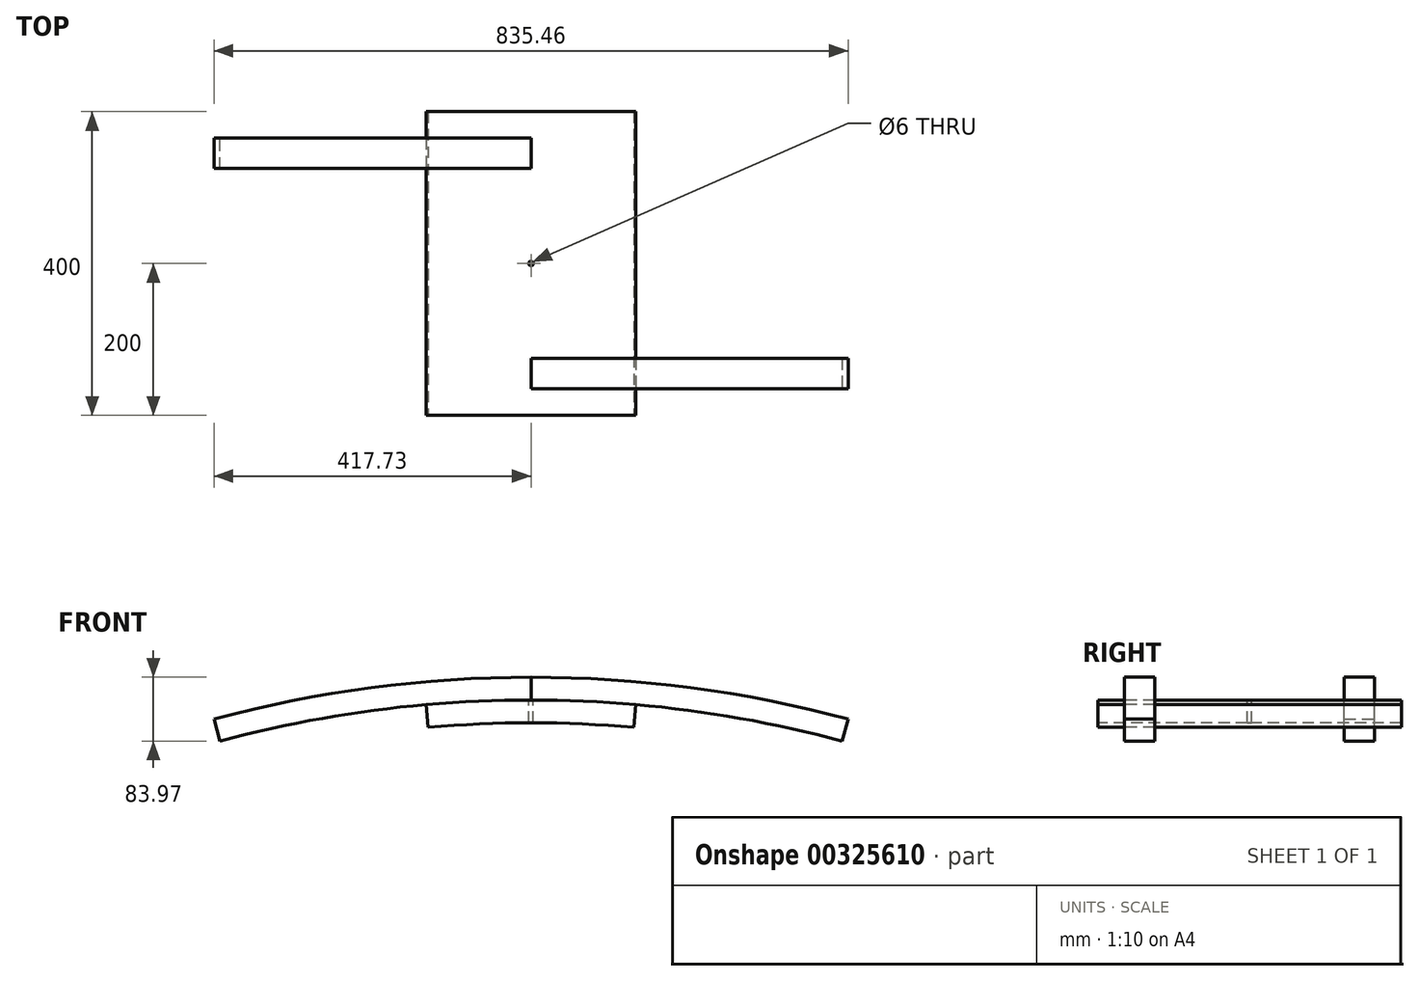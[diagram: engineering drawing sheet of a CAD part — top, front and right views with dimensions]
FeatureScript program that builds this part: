
annotation { "Feature Type Name" : "Feature", "Feature Type Description" : "" }
export const myFeature = defineFeature(function(context is Context, id is Id, definition is map)
    precondition{}
    {
        {
            var Q0;
            Q0=qCreatedBy(makeId("Right.planeOp"),FACE);
            var sketch = newSketch(context, id + "F0", { "sketchPlane" : qUnion([Q0])});
            skLineSegment(sketch, "E0", {"start": v(-75.2, 0) * mm, "end": v(74.8, 0) * mm, "construction": true});
            skLineSegment(sketch, "E1.bottom", {"start": v(200, 1554) * mm, "end": v(-200, 1554) * mm});
            skLineSegment(sketch, "E1.top", {"start": v(200, 1584) * mm, "end": v(-200, 1584) * mm});
            skLineSegment(sketch, "E1.left", {"start": v(200, 1554) * mm, "end": v(200, 1584) * mm});
            skLineSegment(sketch, "E1.right", {"start": v(-200, 1554) * mm, "end": v(-200, 1584) * mm});
            skPoint(sketch, "E1.middle", {"position": v(0, 1569) * mm});
            skSolve(sketch);
        }
        {
            var Q0;
            Q0=makeQuery(id+"F0.imprint","IMPRINT",FACE,{"disambiguationData":[TD([[makeQuery(id+"F0.imprint","IMPRINT",EDGE,{"derivedFrom":sQuery(id+"F0.wireOp",EDGE,"E1.bottom")}),-1.0]])]});
            var Q1;
            Q1=sQuery(id+"F0.wireOp",EDGE,"E0");
            revolve(context, id + "F1", {"entities" : qUnion([Q0]), "axis" : qUnion([Q1]), "revolveType" : RevolveType.SYMMETRIC, "angle" : 10 * degree});
        }
        {
            var Q0;
            Q0=qCreatedBy(makeId("Top.planeOp"),FACE);
            cPlane(context, id + "F2", {"entities" : qUnion([Q0]), "cplaneType" : CPlaneType.OFFSET, "offset" : 1600 * mm, "width" : 150 * mm, "height" : 150 * mm});
        }
        {
            var Q0;
            Q0=qCreatedBy(id+"F2.planeOp",FACE);
            var sketch = newSketch(context, id + "F3", { "sketchPlane" : qUnion([Q0])});
            skCircle(sketch, "E2", {"center": v(-100, 225) * mm, "radius": 3 * mm});
            skLineSegment(sketch, "E3", {"start": v(150.49, 0) * mm, "end": v(-149.91, 0) * mm, "construction": true});
            skLineSegment(sketch, "E4", {"start": v(0, 158.55) * mm, "end": v(0, -163.66) * mm, "construction": true});
            skPoint(sketch, "E5", {"position": v(0, 0) * mm});
            skSolve(sketch);
        }
        {
            var Q0;
            Q0=sQuery(id+"F3.wireOp",VERTEX,"E5");
            var Q1;
            Q1=makeQuery(id+"F1.opRevolve","SWEPT_BODY",BODY,{"disambiguationData":[OSD([sQuery(id+"F0.wireOp",EDGE,"E1.bottom"),sQuery(id+"F0.wireOp",EDGE,"E1.top"),sQuery(id+"F0.wireOp",EDGE,"E1.left"),sQuery(id+"F0.wireOp",EDGE,"E1.right")])]});
            hole(context, id + "F4", {"style" : HoleStyle.SIMPLE, "endStyle" : HoleEndStyle.BLIND, "holeDiameter" : 6 * mm, "holeDepth" : 100 * mm, "tappedDepth" : 12 * mm, "tapClearance" : 3, "startFromSketch" : true, "locations" : qUnion([Q0]), "scope" : qUnion([Q1])});
        }
        {
            var Q0;
            Q0=qCreatedBy(makeId("Right.planeOp"),FACE);
            var sketch = newSketch(context, id + "F5", { "sketchPlane" : qUnion([Q0])});
            skLineSegment(sketch, "E6.bottom", {"start": v(-125, 1584) * mm, "end": v(-165, 1584) * mm});
            skLineSegment(sketch, "E6.top", {"start": v(-125, 1614) * mm, "end": v(-165, 1614) * mm});
            skLineSegment(sketch, "E6.left", {"start": v(-125, 1584) * mm, "end": v(-125, 1614) * mm});
            skLineSegment(sketch, "E6.right", {"start": v(-165, 1584) * mm, "end": v(-165, 1614) * mm});
            skPoint(sketch, "E6.middle", {"position": v(-145, 1599) * mm});
            skLineSegment(sketch, "E7", {"start": v(0, 1548.3) * mm, "end": v(0, 1675.11) * mm, "construction": true});
            skLineSegment(sketch, "E8.MirrorCS", {"start": v(125, 1614) * mm, "end": v(165, 1614) * mm});
            skLineSegment(sketch, "E9.MirrorCS", {"start": v(125, 1584) * mm, "end": v(125, 1614) * mm});
            skLineSegment(sketch, "E10.MirrorCS", {"start": v(125, 1584) * mm, "end": v(165, 1584) * mm});
            skLineSegment(sketch, "E11.MirrorCS", {"start": v(165, 1584) * mm, "end": v(165, 1614) * mm});
            skPoint(sketch, "E12.MirrorP", {"position": v(145, 1599) * mm});
            skSolve(sketch);
        }
        {
            var Q0;
            Q0=makeQuery(id+"F5.imprint","IMPRINT",FACE,{"disambiguationData":[TD([[makeQuery(id+"F5.imprint","IMPRINT",EDGE,{"derivedFrom":sQuery(id+"F5.wireOp",EDGE,"E6.bottom")}),-1.0]])]});
            var Q1;
            Q1=sQuery(id+"F0.wireOp",EDGE,"E0");
            revolve(context, id + "F6", {"entities" : qUnion([Q0]), "axis" : qUnion([Q1]), "revolveType" : RevolveType.ONE_DIRECTION, "angle" : 15 * degree});
        }
        {
            var Q0;
            Q0=makeQuery(id+"F5.imprint","IMPRINT",FACE,{"disambiguationData":[TD([[makeQuery(id+"F5.imprint","IMPRINT",EDGE,{"derivedFrom":sQuery(id+"F5.wireOp",EDGE,"E8.MirrorCS")}),-1.0]])]});
            var Q1;
            Q1=sQuery(id+"F0.wireOp",EDGE,"E0");
            revolve(context, id + "F7", {"entities" : qUnion([Q0]), "axis" : qUnion([Q1]), "revolveType" : RevolveType.ONE_DIRECTION, "oppositeDirection" : true, "angle" : 15 * degree});
        }
    });
